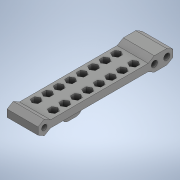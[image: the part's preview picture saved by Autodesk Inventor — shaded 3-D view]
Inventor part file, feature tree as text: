
AUTODESK INVENTOR PART (.ipt)
format: ipt  version: 2020 (Build 240168000, 168)  size: 479,744 bytes
history: native  units: in
note: dims shown in document units (in); Inventor stores cm internally (conversion verified against a paired STEP export)
features: sketch x7, extrude x6, projected_geometry x4, plane x2, mirror x1, fillet x1
ambient origin geometry x8: Origin, YZ Plane, XZ Plane, XY Plane, X Axis, Y Axis, Z Axis, Center Point
bodies: Solid1 (feature_tree)
feature tree (21):
  extrude  "Extrusion1"  Depth=3.4256in
  plane  "Work Plane1"
  extrude  "Extrusion2"  Depth=0.7874in
  sketch  "Sketch4"  dims[d4=0.0in d5=0.0827in]
  extrude  "Extrusion4"  Depth=0.0827in
  plane  "Work Plane2"
  extrude  "Extrusion6"  Depth=3.1106in
  mirror  "Mirror2"
  extrude  "Extrusion7"  Depth=0.315in
  extrude  "Extrusion8"  Depth=0.2362in
  fillet  "Fillet1"  [1 undecoded]
  sketch  "Sketch1"  dims[d0=0.1818in d1=3.4256in]
  sketch  "Sketch2"  dims[d2=0.1378in d3=0.7874in]
  sketch  "Sketch5"  dims[d6=0.7874in d7=0.0in d28=3.1106in]
  sketch  "Sketch7"  dims[d29=0.315in d31=0.315in]
  projected_geometry  "Projected Loop7"
  projected_geometry  "Projected Loop8"
  sketch  "Sketch8"  dims[d33=0.1575in d34=0.2362in d35=0.0in]
  projected_geometry  "Projected Loop9"
  sketch  "Sketch10"  dims[d38=0.315in d39=0.2756in d40=-0.3092in d41=0.0787in d42=0.0787in d43=0.0787in d44=3.1496in d46=0.2913in d47=0.3937in d49=0.3937in d51=3.1496in d53=0.2913in d54=0.3937in d56=0.3937in d58=0.0in d59=0.0in d60=1.0994in d61=0.1378in d63=1.1811in d64=0.1575in d65=0.0in d66=0.126in d67=0.1575in]
  projected_geometry  "Projected Loop10"
note: 1 required parameter value undecoded (feature->parameter linkage not recoverable at this tier; creation-order binding heuristic only, values carry confidence <= 0.55)
